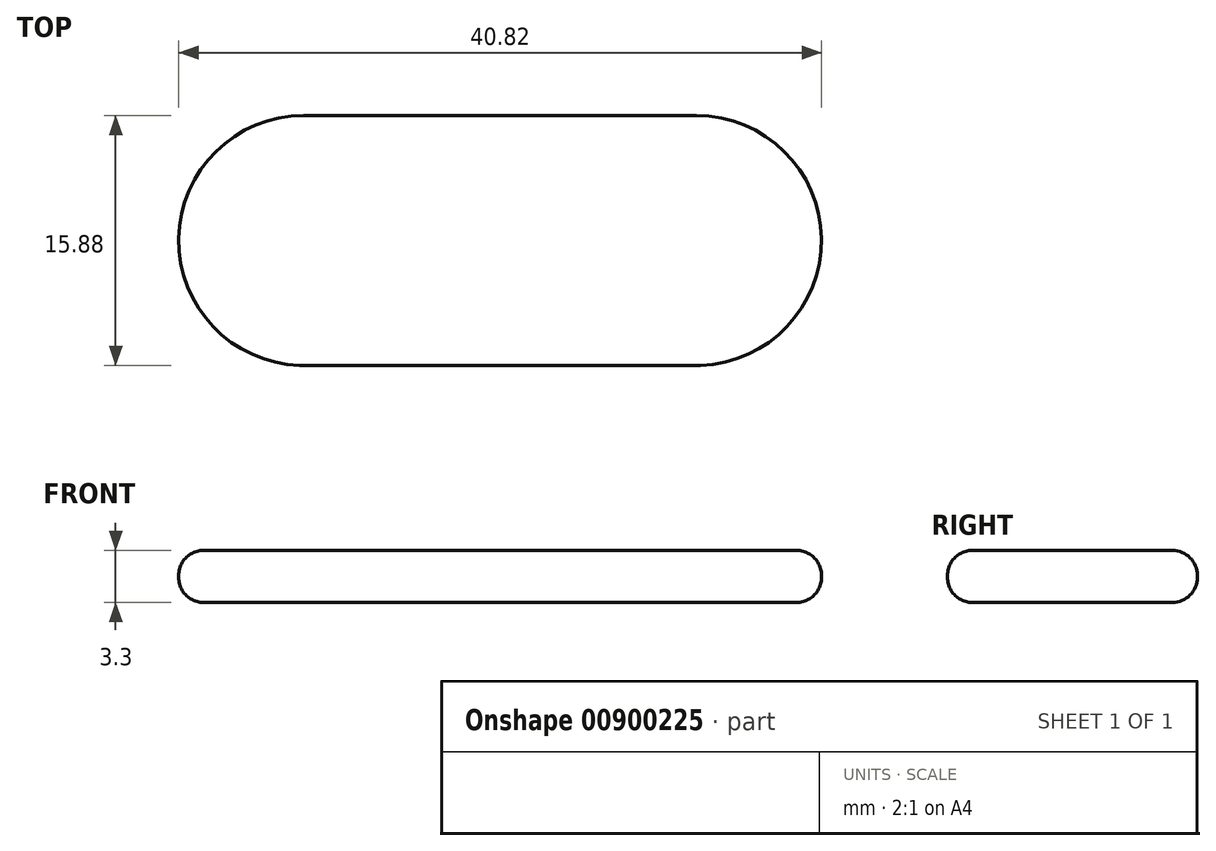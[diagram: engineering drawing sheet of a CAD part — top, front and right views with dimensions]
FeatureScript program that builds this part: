
annotation { "Feature Type Name" : "Feature", "Feature Type Description" : "" }
export const myFeature = defineFeature(function(context is Context, id is Id, definition is map)
    precondition{}
    {
        {
            var Q0;
            Q0=qCreatedBy(makeId("Top.planeOp"),FACE);
            var sketch = newSketch(context, id + "F0", { "sketchPlane" : qUnion([Q0])});
            skLineSegment(sketch, "E0", {"start": v(-33.86, 31.75) * mm, "end": v(-58.8, 31.75) * mm});
            skLineSegment(sketch, "E1", {"start": v(-33.63, 15.88) * mm, "end": v(-59.03, 15.88) * mm});
            skArc(sketch, "E2", {"start": v(-58.8, 31.75) * mm, "mid": v(-66.74, 23.92) * mm, "end": v(-59.03, 15.88) * mm});
            skArc(sketch, "E3", {"start": v(-33.63, 15.88) * mm, "mid": v(-25.92, 23.92) * mm, "end": v(-33.86, 31.75) * mm});
            skSolve(sketch);
        }
        {
            var Q0;
            Q0=makeQuery(id+"F0.imprint","IMPRINT",FACE,{"disambiguationData":[TD([[makeQuery(id+"F0.imprint","IMPRINT",EDGE,{"derivedFrom":sQuery(id+"F0.wireOp",EDGE,"E0")}),1.0]])]});
            extrude(context, id + "F1", {"entities" : qUnion([Q0]), "depth" : 3.3 * mm});
        }
        {
            var Q0;
            Q0=makeQuery(id+"F1.opExtrude","CAP_EDGE",EDGE,{"disambiguationData":[OSD([sQuery(id+"F0.wireOp",EDGE,"E2")])],"isStart":true});
            var Q1;
            Q1=makeQuery(id+"F1.opExtrude","CAP_EDGE",EDGE,{"disambiguationData":[OSD([sQuery(id+"F0.wireOp",EDGE,"E0")])],"isStart":true});
            var Q2;
            Q2=makeQuery(id+"F1.opExtrude","SWEPT_FACE",FACE,{"disambiguationData":[OSD([sQuery(id+"F0.wireOp",EDGE,"E2")])]});
            var Q3;
            Q3=makeQuery(id+"F1.opExtrude","CAP_EDGE",EDGE,{"disambiguationData":[OSD([sQuery(id+"F0.wireOp",EDGE,"E3")])],"isStart":false});
            var Q4;
            Q4=makeQuery(id+"F1.opExtrude","CAP_EDGE",EDGE,{"disambiguationData":[OSD([sQuery(id+"F0.wireOp",EDGE,"E3")])],"isStart":true});
            var Q5;
            Q5=makeQuery(id+"F1.opExtrude","CAP_FACE",FACE,{"disambiguationData":[OSD([sQuery(id+"F0.wireOp",EDGE,"E0"),sQuery(id+"F0.wireOp",EDGE,"E1"),sQuery(id+"F0.wireOp",EDGE,"E2"),sQuery(id+"F0.wireOp",EDGE,"E3")])],"isStart":true});
            var Q6;
            Q6=makeQuery(id+"F1.opExtrude","CAP_FACE",FACE,{"disambiguationData":[OSD([sQuery(id+"F0.wireOp",EDGE,"E0"),sQuery(id+"F0.wireOp",EDGE,"E1"),sQuery(id+"F0.wireOp",EDGE,"E2"),sQuery(id+"F0.wireOp",EDGE,"E3")])],"isStart":false});
            var Q7;
            Q7=makeQuery(id+"F1.opExtrude","SWEPT_FACE",FACE,{"disambiguationData":[OSD([sQuery(id+"F0.wireOp",EDGE,"E1")])]});
            var Q8;
            Q8=makeQuery(id+"F1.opExtrude","SWEPT_FACE",FACE,{"disambiguationData":[OSD([sQuery(id+"F0.wireOp",EDGE,"E3")])]});
            var Q9;
            Q9=makeQuery(id+"F1.opExtrude","CAP_EDGE",EDGE,{"disambiguationData":[OSD([sQuery(id+"F0.wireOp",EDGE,"E2")])],"isStart":false});
            var Q10;
            Q10=makeQuery(id+"F1.opExtrude","SWEPT_FACE",FACE,{"disambiguationData":[OSD([sQuery(id+"F0.wireOp",EDGE,"E0")])]});
            var Q11;
            Q11=makeQuery(id+"F1.opExtrude","CAP_EDGE",EDGE,{"disambiguationData":[OSD([sQuery(id+"F0.wireOp",EDGE,"E1")])],"isStart":false});
            var Q12;
            Q12=makeQuery(id+"F1.opExtrude","SWEPT_EDGE",EDGE,{"disambiguationData":[OSD([sQuery(id+"F0.wireOp",EDGE,"E0"),sQuery(id+"F0.wireOp",EDGE,"E3")])]});
            var Q13;
            Q13=makeQuery(id+"F1.opExtrude","CAP_EDGE",EDGE,{"disambiguationData":[OSD([sQuery(id+"F0.wireOp",EDGE,"E1")])],"isStart":true});
            var Q14;
            Q14=makeQuery(id+"F1.opExtrude","SWEPT_EDGE",EDGE,{"disambiguationData":[OSD([sQuery(id+"F0.wireOp",EDGE,"E0"),sQuery(id+"F0.wireOp",EDGE,"E2")])]});
            var Q15;
            Q15=makeQuery(id+"F1.opExtrude","SWEPT_EDGE",EDGE,{"disambiguationData":[OSD([sQuery(id+"F0.wireOp",EDGE,"E1"),sQuery(id+"F0.wireOp",EDGE,"E2")])]});
            var Q16;
            Q16=makeQuery(id+"F1.opExtrude","CAP_EDGE",EDGE,{"disambiguationData":[OSD([sQuery(id+"F0.wireOp",EDGE,"E0")])],"isStart":false});
            fillet(context, id + "F2", {"entities" : qUnion([Q0, Q1, Q2, Q3, Q4, Q5, Q6, Q7, Q8, Q9, Q10, Q11, Q12, Q13, Q14, Q15, Q16]), "radius" : 1.59 * mm, "tangentPropagation" : true, "allowEdgeOverflow" : false});
        }
    });
